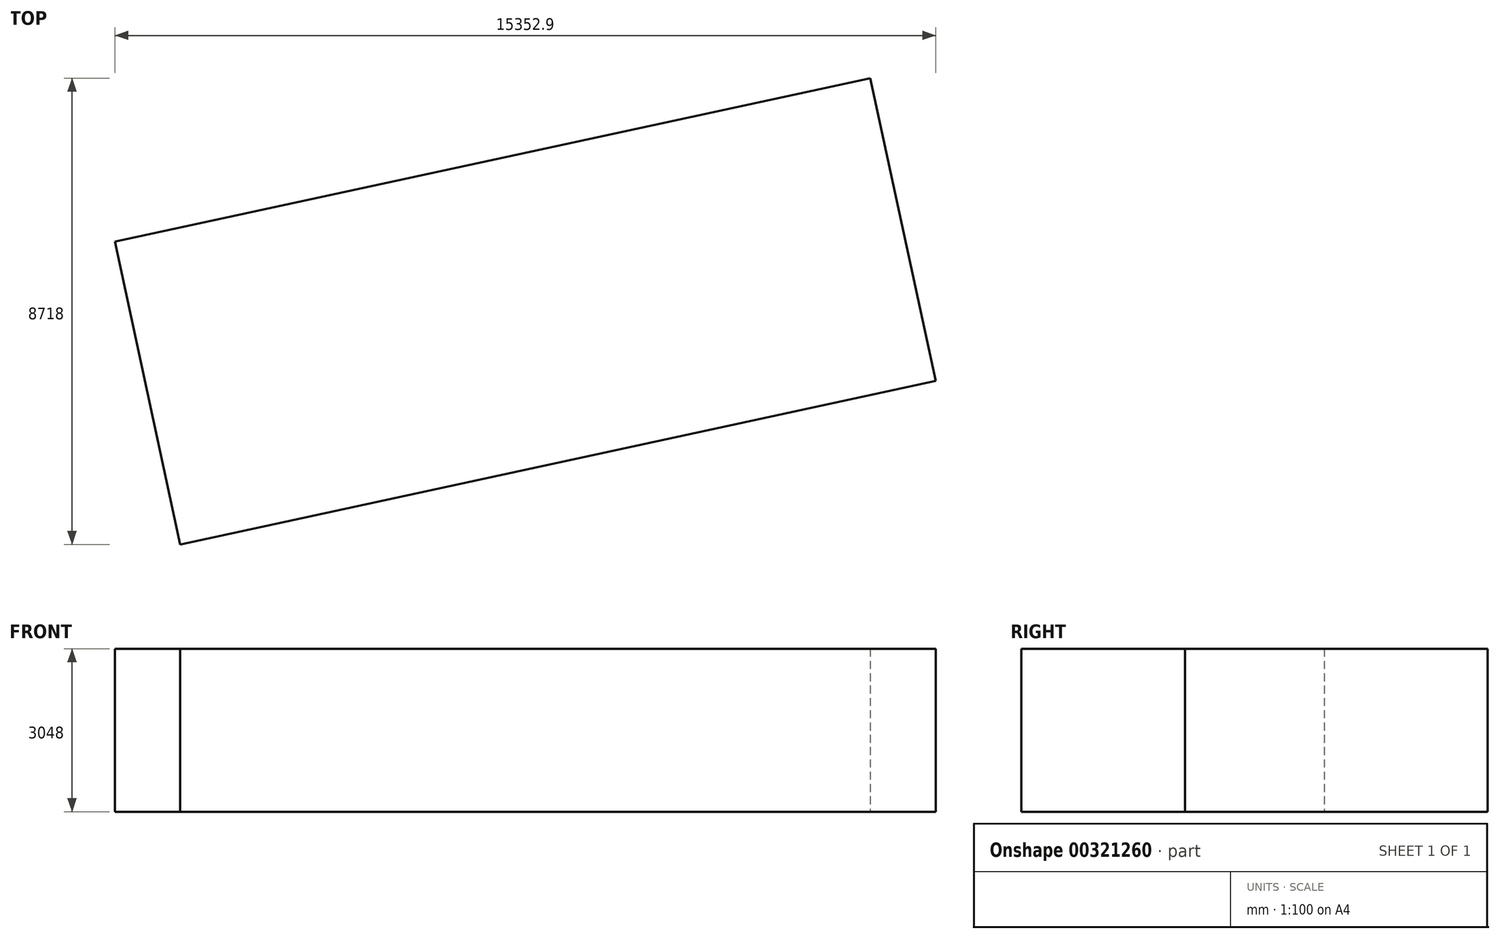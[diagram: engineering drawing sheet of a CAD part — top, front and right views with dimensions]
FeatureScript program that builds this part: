
annotation { "Feature Type Name" : "Feature", "Feature Type Description" : "" }
export const myFeature = defineFeature(function(context is Context, id is Id, definition is map)
    precondition{}
    {
        {
            var Q0;
            Q0=qCreatedBy(makeId("Top.planeOp"),FACE);
            var sketch = newSketch(context, id + "F0", { "sketchPlane" : qUnion([Q0])});
            skLineSegment(sketch, "E0", {"start": v(0, 0) * mm, "end": v(0, 52425.6) * mm});
            skLineSegment(sketch, "E1", {"start": v(0, 52425.6) * mm, "end": v(21448.94, 57068.06) * mm});
            skLineSegment(sketch, "E2", {"start": v(21448.94, 57068.06) * mm, "end": v(21448.94, 4642.46) * mm});
            skLineSegment(sketch, "E3", {"start": v(21448.94, 4642.46) * mm, "end": v(0, 0) * mm});
            skLineSegment(sketch, "E4.0", {"start": v(3048, 45288.87) * mm, "end": v(18400.94, 48611.9) * mm});
            skLineSegment(sketch, "E5.0", {"start": v(3048, 659.72) * mm, "end": v(3048, 53085.32) * mm});
            skLineSegment(sketch, "E6.0", {"start": v(18400.94, 56408.34) * mm, "end": v(18400.94, 4642.46) * mm});
            skLineSegment(sketch, "E7.0", {"start": v(3048, 39363.57) * mm, "end": v(18400.94, 42686.6) * mm});
            skLineSegment(sketch, "E8", {"start": v(11695.34, 41235.22) * mm, "end": v(18400.94, 41235.22) * mm});
            skLineSegment(sketch, "E9.0", {"start": v(11695.34, 34529.62) * mm, "end": v(18400.94, 34529.62) * mm});
            skLineSegment(sketch, "E10.trimOffspring", {"start": v(11695.34, 41235.22) * mm, "end": v(11695.34, 34529.62) * mm});
            skLineSegment(sketch, "E11", {"start": v(18400.94, 42686.6) * mm, "end": v(17175.85, 48346.73) * mm});
            skLineSegment(sketch, "E12", {"start": v(3048, 45288.87) * mm, "end": v(4273.1, 39628.73) * mm});
            skText(sketch, "E13", { "text": "Garage", "fontName": "OpenSans-Regular.ttf"});
            const initialGuessF0  = {"E13": [13.8137, 37.74744, 1, 0, 0.62029]};
            skSetInitialGuess(sketch, initialGuessF0);
            skSolve(sketch);
        }
        {
            var Q0;
            {var subQ0=sQuery(id+"F0.wireOp",EDGE,"E11");Q0=makeQuery(id+"F0.imprint","IMPRINT",FACE,{"disambiguationData":[TD([[makeQuery(id+"F0.imprint","IMPRINT",EDGE,{"derivedFrom":subQ0}),1.0]])]});}
            extrude(context, id + "F1", {"entities" : qUnion([Q0]), "depth" : 3048 * mm});
        }
    });
